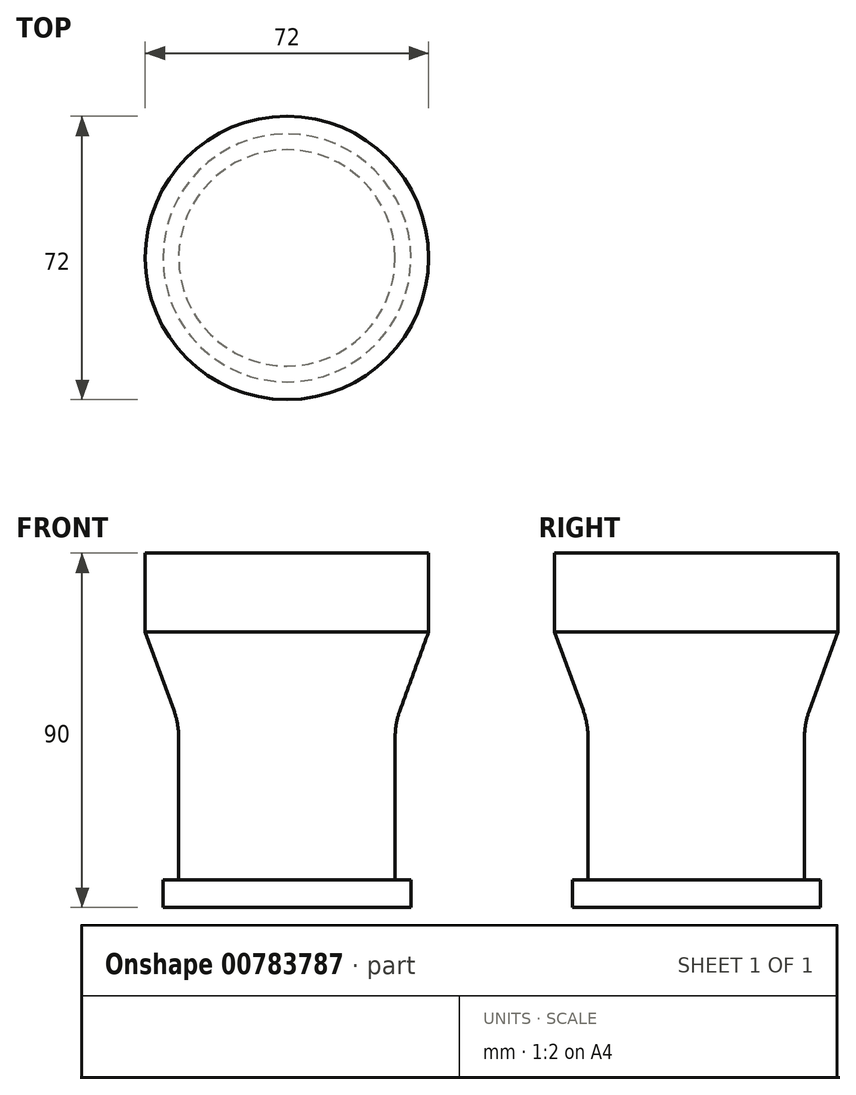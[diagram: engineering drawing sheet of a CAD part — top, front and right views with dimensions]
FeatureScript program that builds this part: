
annotation { "Feature Type Name" : "Feature", "Feature Type Description" : "" }
export const myFeature = defineFeature(function(context is Context, id is Id, definition is map)
    precondition{}
    {
        {
            var Q0;
            Q0=qCreatedBy(makeId("Front.planeOp"),FACE);
            var sketch = newSketch(context, id + "F0", { "sketchPlane" : qUnion([Q0])});
            skLineSegment(sketch, "E0", {"start": v(0, 16.52) * mm, "end": v(0, -70.06) * mm, "construction": true});
            skLineSegment(sketch, "E1", {"start": v(0, 0) * mm, "end": v(-36, 0) * mm});
            skLineSegment(sketch, "E2", {"start": v(-36, 0) * mm, "end": v(-36, -20) * mm});
            skLineSegment(sketch, "E3", {"start": v(-36, -20) * mm, "end": v(-27.5, -43.35) * mm});
            skLineSegment(sketch, "E4", {"start": v(-27.5, -43.35) * mm, "end": v(-27.5, -83) * mm});
            skLineSegment(sketch, "E5", {"start": v(-27.5, -83) * mm, "end": v(-31.5, -83) * mm});
            skLineSegment(sketch, "E6", {"start": v(-31.5, -83) * mm, "end": v(-31.5, -90) * mm});
            skLineSegment(sketch, "E7", {"start": v(-31.5, -90) * mm, "end": v(0, -90) * mm});
            skLineSegment(sketch, "E8", {"start": v(0, -90) * mm, "end": v(0, 0) * mm});
            skSolve(sketch);
        }
        {
            var Q0;
            Q0=makeQuery(id+"F0.imprint","IMPRINT",FACE,{"disambiguationData":[TD([[makeQuery(id+"F0.imprint","IMPRINT",EDGE,{"derivedFrom":sQuery(id+"F0.wireOp",EDGE,"E1")}),1.0]])]});
            var Q1;
            Q1=sQuery(id+"F0.wireOp",EDGE,"E0");
            revolve(context, id + "F1", {"surfaceOperationType" : NewSurfaceOperationType.NEW, "entities" : qUnion([Q0]), "axis" : qUnion([Q1]), "revolveType" : RevolveType.FULL});
        }
        {
            var Q0;
            Q0=makeQuery(id+"F1.opRevolve","SWEPT_EDGE",EDGE,{"disambiguationData":[OSD([sQuery(id+"F0.wireOp",EDGE,"E3"),sQuery(id+"F0.wireOp",EDGE,"E4")])]});
            fillet(context, id + "F2", {"entities" : qUnion([Q0]), "radius" : 20 * mm, "tangentPropagation" : true, "allowEdgeOverflow" : false});
        }
    });
